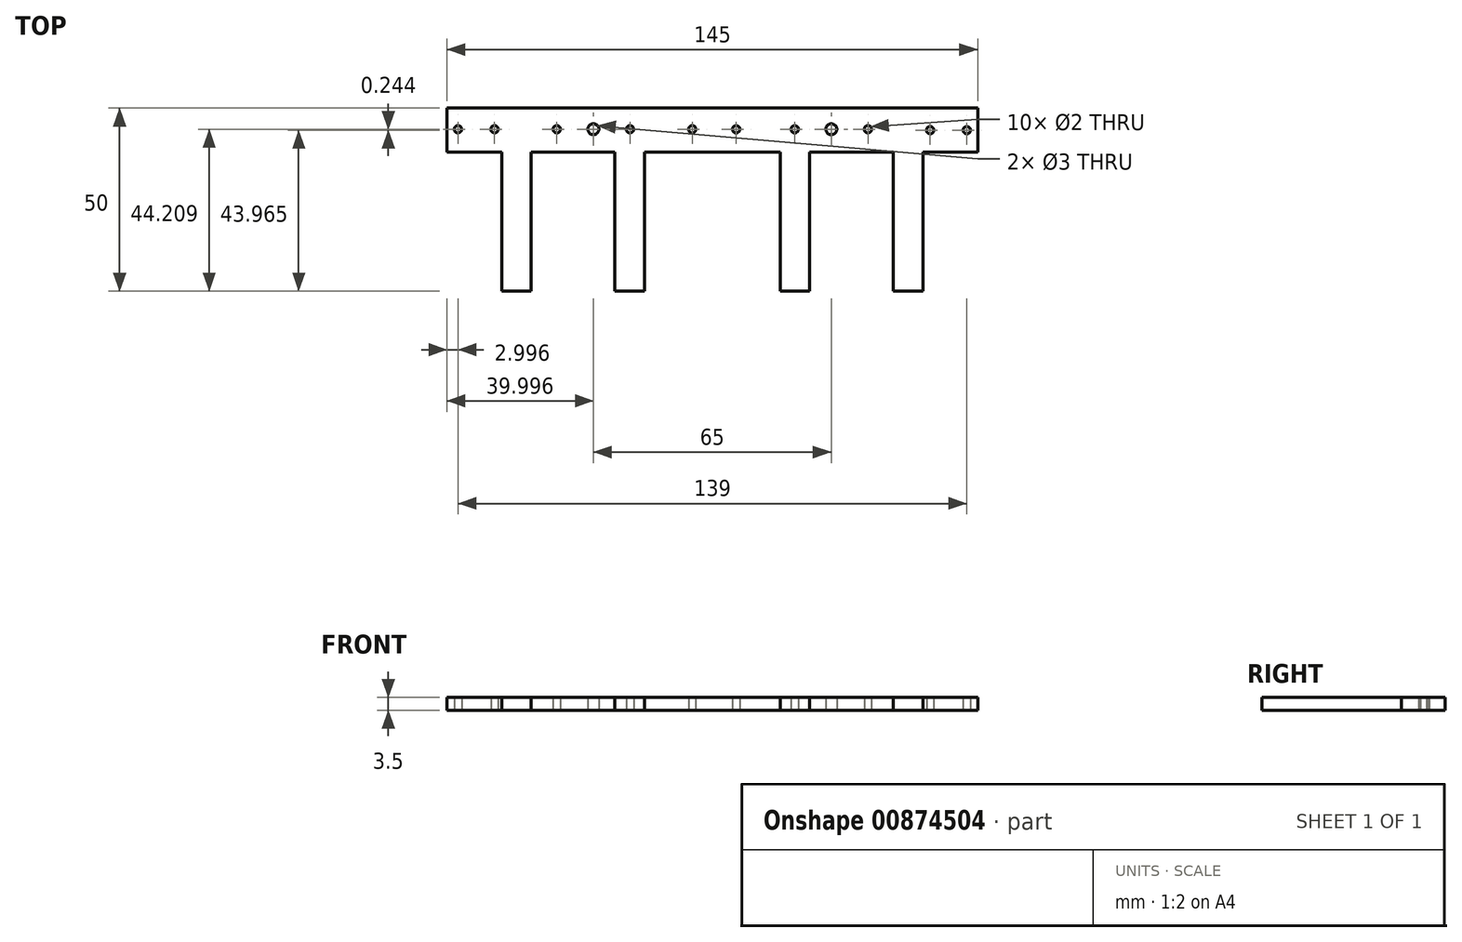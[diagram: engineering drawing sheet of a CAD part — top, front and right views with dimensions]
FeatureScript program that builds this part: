
annotation { "Feature Type Name" : "Feature", "Feature Type Description" : "" }
export const myFeature = defineFeature(function(context is Context, id is Id, definition is map)
    precondition{}
    {
        {
            var Q0;
            Q0=qCreatedBy(makeId("Top.planeOp"),FACE);
            var sketch = newSketch(context, id + "F0", { "sketchPlane" : qUnion([Q0])});
            skLineSegment(sketch, "E0", {"start": v(-69.1, 27.57) * mm, "end": v(75.9, 27.57) * mm});
            skLineSegment(sketch, "E1.left", {"start": v(-69.1, 27.57) * mm, "end": v(-69.1, 15.57) * mm});
            skLineSegment(sketch, "E1.right", {"start": v(75.9, 27.57) * mm, "end": v(75.9, 15.57) * mm});
            skPoint(sketch, "E2", {"position": v(-69.1, 15.57) * mm});
            skPoint(sketch, "E3", {"position": v(75.9, 15.57) * mm});
            skPoint(sketch, "E4", {"position": v(75.9, 27.57) * mm});
            skPoint(sketch, "E5", {"position": v(-69.1, 27.57) * mm});
            skLineSegment(sketch, "E6", {"start": v(-69.1, 15.57) * mm, "end": v(75.9, 15.57) * mm});
            skPoint(sketch, "E7", {"position": v(-54.1, 15.57) * mm});
            skPoint(sketch, "E8", {"position": v(60.9, 15.57) * mm});
            skPoint(sketch, "E9", {"position": v(-46.1, 15.57) * mm});
            skPoint(sketch, "E10", {"position": v(52.9, 15.57) * mm});
            skPoint(sketch, "E11", {"position": v(-23.1, 15.57) * mm});
            skPoint(sketch, "E12", {"position": v(29.9, 15.57) * mm});
            skPoint(sketch, "E13", {"position": v(-15.1, 15.57) * mm});
            skPoint(sketch, "E14", {"position": v(21.9, 15.57) * mm});
            skLineSegment(sketch, "E15.bottom", {"start": v(-46.1, 15.57) * mm, "end": v(-54.1, 15.57) * mm});
            skLineSegment(sketch, "E15.top", {"start": v(-46.1, -22.43) * mm, "end": v(-54.1, -22.43) * mm});
            skLineSegment(sketch, "E15.left", {"start": v(-46.1, 15.57) * mm, "end": v(-46.1, -22.43) * mm});
            skLineSegment(sketch, "E15.right", {"start": v(-54.1, 15.57) * mm, "end": v(-54.1, -22.43) * mm});
            skLineSegment(sketch, "E16.bottom", {"start": v(-15.1, 15.57) * mm, "end": v(-23.2, 15.57) * mm});
            skLineSegment(sketch, "E16.top", {"start": v(-15.1, -22.43) * mm, "end": v(-23.2, -22.43) * mm});
            skLineSegment(sketch, "E16.left", {"start": v(-15.1, 15.57) * mm, "end": v(-15.1, -22.43) * mm});
            skLineSegment(sketch, "E16.right", {"start": v(-23.2, 15.57) * mm, "end": v(-23.2, -22.43) * mm});
            skLineSegment(sketch, "E17.bottom", {"start": v(29.9, 15.57) * mm, "end": v(21.9, 15.57) * mm});
            skLineSegment(sketch, "E17.top", {"start": v(29.9, -22.43) * mm, "end": v(21.9, -22.43) * mm});
            skLineSegment(sketch, "E17.left", {"start": v(29.9, 15.57) * mm, "end": v(29.9, -22.43) * mm});
            skLineSegment(sketch, "E17.right", {"start": v(21.9, 15.57) * mm, "end": v(21.9, -22.43) * mm});
            skLineSegment(sketch, "E18.bottom", {"start": v(60.9, 15.57) * mm, "end": v(52.88, 15.57) * mm});
            skLineSegment(sketch, "E18.top", {"start": v(60.9, -22.43) * mm, "end": v(52.88, -22.43) * mm});
            skLineSegment(sketch, "E18.left", {"start": v(60.9, 15.57) * mm, "end": v(60.9, -22.43) * mm});
            skLineSegment(sketch, "E18.right", {"start": v(52.88, 15.57) * mm, "end": v(52.88, -22.43) * mm});
            skPoint(sketch, "E19", {"position": v(-66.1, 21.78) * mm});
            skPoint(sketch, "E20", {"position": v(-56.1, 21.78) * mm});
            skPoint(sketch, "E21", {"position": v(72.9, 21.53) * mm});
            skPoint(sketch, "E22", {"position": v(62.9, 21.53) * mm});
            skLineSegment(sketch, "E23", {"start": v(-69.1, 21.78) * mm, "end": v(75.9, 21.78) * mm});
            skPoint(sketch, "E24", {"position": v(-39.1, 21.78) * mm});
            skPoint(sketch, "E25", {"position": v(-29.1, 21.78) * mm});
            skPoint(sketch, "E26", {"position": v(-19.1, 21.78) * mm});
            skPoint(sketch, "E27", {"position": v(-2.1, 21.78) * mm});
            skPoint(sketch, "E28", {"position": v(9.9, 21.78) * mm});
            skPoint(sketch, "E29", {"position": v(25.9, 21.78) * mm});
            skPoint(sketch, "E30", {"position": v(35.9, 21.78) * mm});
            skPoint(sketch, "E31", {"position": v(45.9, 21.78) * mm});
            skLineSegment(sketch, "E32", {"start": v(-66.14, 27.57) * mm, "end": v(-66.14, 15.57) * mm});
            skLineSegment(sketch, "E33", {"start": v(-55.88, 27.57) * mm, "end": v(-55.88, 15.57) * mm});
            skLineSegment(sketch, "E34", {"start": v(-39.02, 27.57) * mm, "end": v(-39.02, 15.57) * mm});
            skLineSegment(sketch, "E35", {"start": v(-1.88, 27.57) * mm, "end": v(-1.88, 15.57) * mm});
            skLineSegment(sketch, "E36", {"start": v(9.84, 27.57) * mm, "end": v(9.9, 15.57) * mm});
            skLineSegment(sketch, "E37", {"start": v(62.86, 27.57) * mm, "end": v(62.86, 15.57) * mm});
            skLineSegment(sketch, "E38", {"start": v(72.64, 27.57) * mm, "end": v(72.9, 15.57) * mm});
            skPoint(sketch, "E39", {"position": v(-50.34, 15.57) * mm});
            skPoint(sketch, "E40", {"position": v(-19.14, 15.57) * mm});
            skPoint(sketch, "E41", {"position": v(25.9, 15.57) * mm});
            skPoint(sketch, "E42", {"position": v(-50.05, 27.57) * mm});
            skPoint(sketch, "E43", {"position": v(-19.54, 27.57) * mm});
            skPoint(sketch, "E44", {"position": v(26.37, 27.57) * mm});
            skPoint(sketch, "E45", {"position": v(56.88, 27.57) * mm});
            skSolve(sketch);
        }
        {
            var Q0;
            Q0=qSketchRegion(id+"F0",true);
            extrude(context, id + "F1", {"entities" : qUnion([Q0]), "depth" : 3.5 * mm, "offsetDistance" : 25 * mm});
        }
        {
            var Q0;
            Q0=sQuery(id+"F0.wireOp",VERTEX,"E19");
            var Q1;
            Q1=sQuery(id+"F0.wireOp",VERTEX,"E20");
            var Q2;
            Q2=sQuery(id+"F0.wireOp",VERTEX,"E24");
            var Q3;
            Q3=sQuery(id+"F0.wireOp",VERTEX,"E26");
            var Q4;
            Q4=sQuery(id+"F0.wireOp",VERTEX,"E27");
            var Q5;
            Q5=sQuery(id+"F0.wireOp",VERTEX,"E28");
            var Q6;
            Q6=sQuery(id+"F0.wireOp",VERTEX,"E29");
            var Q7;
            Q7=sQuery(id+"F0.wireOp",VERTEX,"E31");
            var Q8;
            Q8=sQuery(id+"F0.wireOp",VERTEX,"E22");
            var Q9;
            Q9=sQuery(id+"F0.wireOp",VERTEX,"E21");
            var Q10;
            Q10=sQuery(id+"F0.wireOp",VERTEX,"8c726180-273c-4d04-a7c9-0866a189a60c");
            var Q11;
            Q11=sQuery(id+"F0.wireOp",VERTEX,"e39a8fda-e123-4ba4-9d9b-40c01698fc2a");
            var Q12;
            Q12=sQuery(id+"F0.wireOp",VERTEX,"e982f95e-ae75-4426-b1ac-4c09b998508d");
            var Q13;
            Q13=sQuery(id+"F0.wireOp",VERTEX,"fcf3facc-e70c-408c-938b-b1fd678deac2");
            var Q14;
            Q14=makeQuery(id+"F1.opExtrude","SWEPT_BODY",BODY,{"disambiguationData":[OSD([sQuery(id+"F0.wireOp",EDGE,"E0"),sQuery(id+"F0.wireOp",EDGE,"E1.left"),sQuery(id+"F0.wireOp",EDGE,"E1.right"),sQuery(id+"F0.wireOp",EDGE,"E6"),sQuery(id+"F0.wireOp",EDGE,"E15.top"),sQuery(id+"F0.wireOp",EDGE,"E15.left"),sQuery(id+"F0.wireOp",EDGE,"E15.right"),sQuery(id+"F0.wireOp",EDGE,"E16.top"),sQuery(id+"F0.wireOp",EDGE,"E16.left"),sQuery(id+"F0.wireOp",EDGE,"E16.right"),sQuery(id+"F0.wireOp",EDGE,"E17.top"),sQuery(id+"F0.wireOp",EDGE,"E17.left"),sQuery(id+"F0.wireOp",EDGE,"E17.right"),sQuery(id+"F0.wireOp",EDGE,"E18.top"),sQuery(id+"F0.wireOp",EDGE,"E18.left"),sQuery(id+"F0.wireOp",EDGE,"E18.right")])]});
            hole(context, id + "F2", {"style" : HoleStyle.SIMPLE, "endStyle" : HoleEndStyle.THROUGH, "oppositeDirection" : true, "holeDiameter" : 2 * mm, "majorDiameter" : 5 * mm, "isTappedThrough" : true, "tappedDepth" : 12 * mm, "tapClearance" : 3, "locations" : qUnion([Q0, Q1, Q2, Q3, Q4, Q5, Q6, Q7, Q8, Q9, Q10, Q11, Q12, Q13]), "scope" : qUnion([Q14])});
        }
        {
            var Q0;
            Q0=sQuery(id+"F0.wireOp",VERTEX,"E25");
            var Q1;
            Q1=sQuery(id+"F0.wireOp",VERTEX,"E30");
            var Q2;
            Q2=makeQuery(id+"F1.opExtrude","SWEPT_BODY",BODY,{"disambiguationData":[OSD([sQuery(id+"F0.wireOp",EDGE,"E0"),sQuery(id+"F0.wireOp",EDGE,"E1.left"),sQuery(id+"F0.wireOp",EDGE,"E1.right"),sQuery(id+"F0.wireOp",EDGE,"E6"),sQuery(id+"F0.wireOp",EDGE,"E15.top"),sQuery(id+"F0.wireOp",EDGE,"E15.left"),sQuery(id+"F0.wireOp",EDGE,"E15.right"),sQuery(id+"F0.wireOp",EDGE,"E16.top"),sQuery(id+"F0.wireOp",EDGE,"E16.left"),sQuery(id+"F0.wireOp",EDGE,"E16.right"),sQuery(id+"F0.wireOp",EDGE,"E17.top"),sQuery(id+"F0.wireOp",EDGE,"E17.left"),sQuery(id+"F0.wireOp",EDGE,"E17.right"),sQuery(id+"F0.wireOp",EDGE,"E18.top"),sQuery(id+"F0.wireOp",EDGE,"E18.left"),sQuery(id+"F0.wireOp",EDGE,"E18.right")])]});
            hole(context, id + "F3", {"style" : HoleStyle.SIMPLE, "endStyle" : HoleEndStyle.THROUGH, "oppositeDirection" : true, "holeDiameter" : 3 * mm, "majorDiameter" : 5 * mm, "isTappedThrough" : true, "tappedDepth" : 12 * mm, "tapClearance" : 3, "locations" : qUnion([Q0, Q1]), "scope" : qUnion([Q2])});
        }
    });
